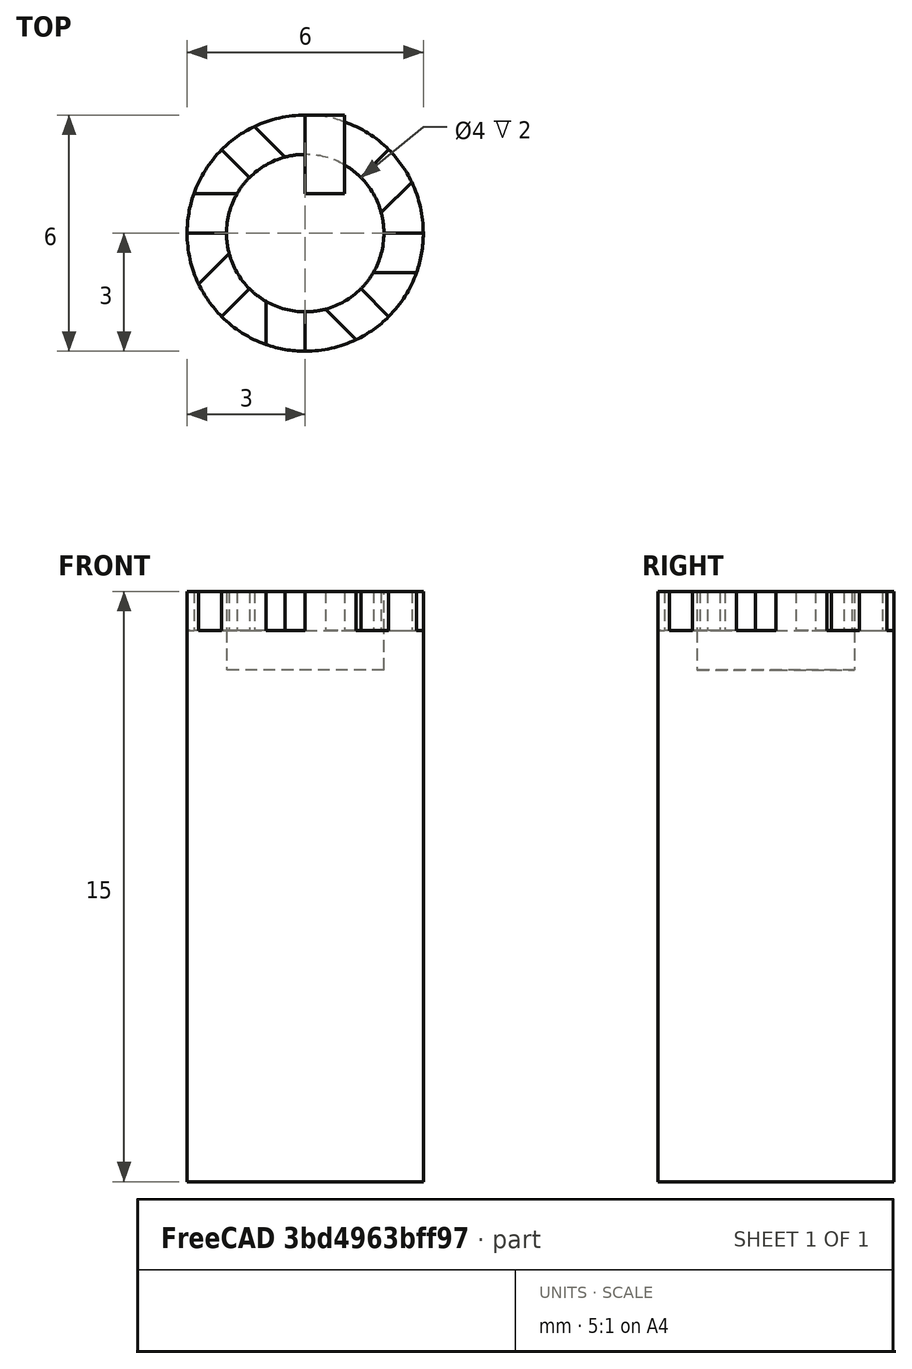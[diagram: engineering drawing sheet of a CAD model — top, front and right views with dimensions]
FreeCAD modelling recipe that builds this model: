
FCSTD DOCUMENT  (FreeCAD 0.20R29177 (Git))
Label: Ejercicio3Video11
License: All rights reserved
LicenseURL: http://en.wikipedia.org/wiki/All_rights_reserved
objects: Part::Cylinder×2, Part::Cut×2, Part::Box×1, Part::FeaturePython×1
note: 5 computed .brp shape members not serialized (recipe doc carries the construction recipe); baked Part::Feature solids carry a one-line shape summary decoded from their .brp

FEATURE [Part::Cylinder] Cylinder  label="Base"
  Angle = 360
  AttacherType = Attacher::AttachEngine3D
  FirstAngle = 0
  Height = 15
  Radius = 3
  SecondAngle = 0
FEATURE [Part::Cylinder] Cylinder001  label="Cilindro"
  Angle = 360
  AttacherType = Attacher::AttachEngine3D
  FirstAngle = 0
  Height = 10
  Placement = pos=(0,0,13) rot=(0,0,1;0rad)
  Radius = 2
  SecondAngle = 0
FEATURE [Part::Cut] Cut
  Base = -> Cylinder
  Tool = -> Cylinder001
FEATURE [Part::Box] Box  label="Cubo"
  AttacherType = Attacher::AttachEngine3D
  Height = 1
  Length = 1
  Placement = pos=(0,1,14) rot=(0,0,1;0rad)
  Width = 2
FEATURE [Part::FeaturePython] Array  # Draft array (typed FeaturePython)
  AlwaysSyncPlacement = false
  Angle = 360
  ArrayType = 1
  Axis = (0,0,1)
  Base = -> Box
  Center = (0,0,0)
  Count = 8
  ExpandArray = false
  Fuse = false
  IntervalAxis = (0,0,0)
  IntervalX = (100,0,0)
  IntervalY = (0,100,0)
  IntervalZ = (0,0,100)
  NumberCircles = 3
  NumberPolar = 8
  NumberX = 2
  NumberY = 2
  NumberZ = 1
  PlacementList = 8 placements: [(0,1,14),(-0.707107,0.707107,14),(-1,2.22045e-16,14),(-0.707107,-0.707107,14),(-1.22465e-16,-1,14),(0.707107,-0.707107,14),(1,-2.22045e-16,14),(0.707107,0.707107,14)]
  RadialDistance = 50
  ScaleList = (8) [(1,1,1),(1,1,1),(1,1,1),(1,1,1),(1,1,1),(1,1,1),(1,1,1),(1,1,1)]
  Symmetry = 1
  TangentialDistance = 25
FEATURE [Part::Cut] Cut001
  Base = -> Cut
  Tool = -> Array
